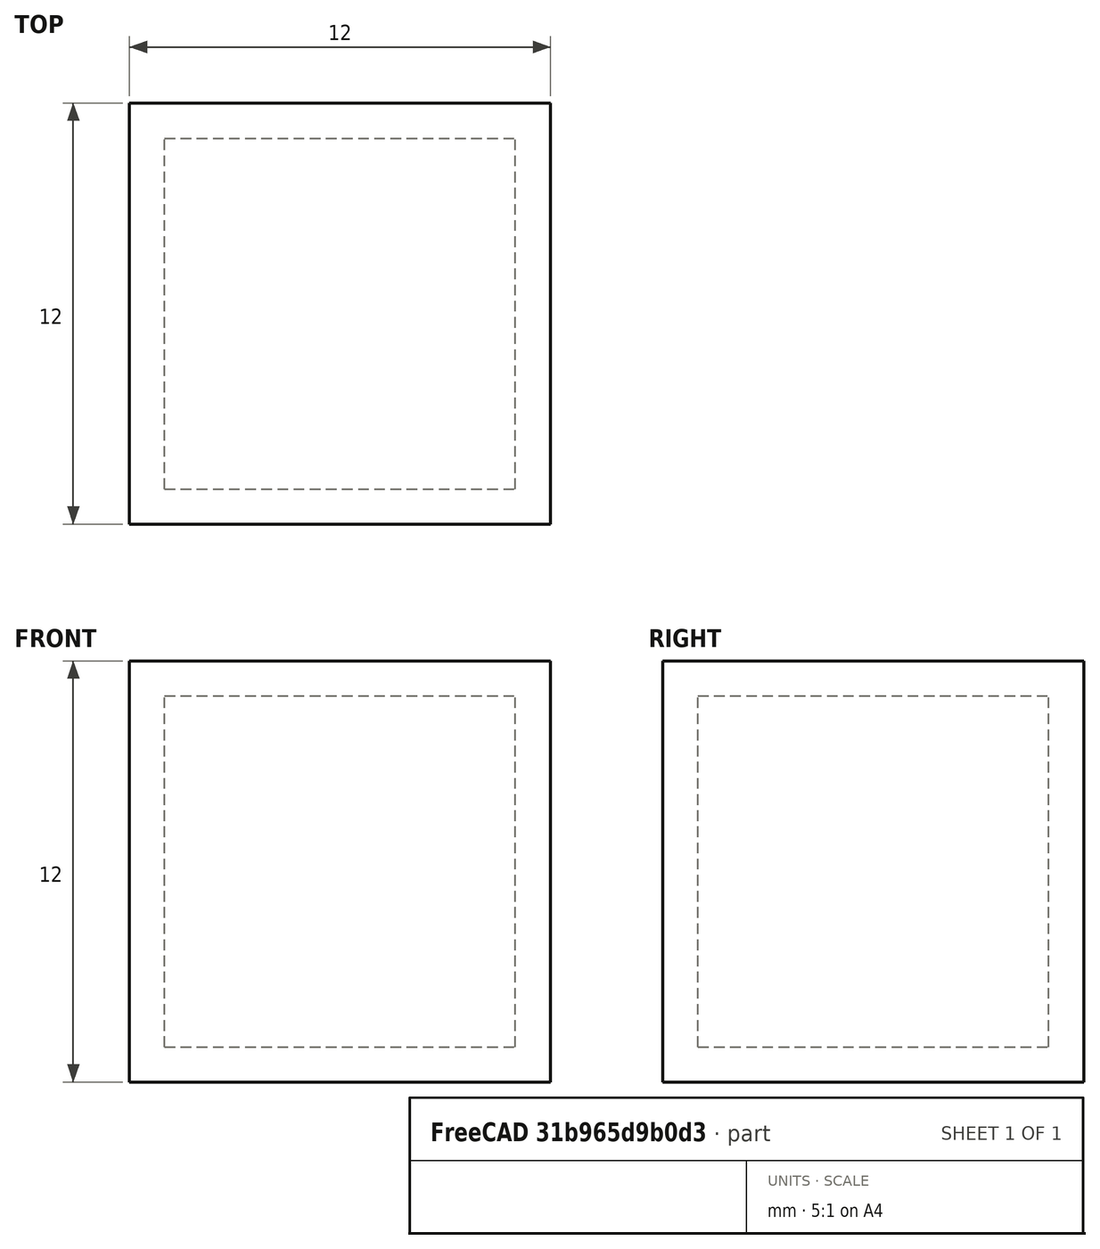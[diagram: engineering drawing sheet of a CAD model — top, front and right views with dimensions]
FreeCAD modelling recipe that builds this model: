
FCSTD DOCUMENT  (FreeCAD 0.17R12135 +10 (Git))
Label: boxtest
License: All rights reserved
LicenseURL: http://en.wikipedia.org/wiki/All_rights_reserved
objects: Path::FeaturePython×3, Part::FeaturePython×2, Part::Box×1, Path::FeatureCompoundPython×1
note: 4 computed .brp shape members not serialized (recipe doc carries the construction recipe); baked Part::Feature solids carry a one-line shape summary decoded from their .brp

FEATURE [Part::Box] Box  label="Cube"
  AttacherType = Attacher::AttachEngine3D
  Height = 10
  Length = 10
  Width = 10
FEATURE [Part::FeaturePython] Clone  label="Base-Cube"  # Draft clone (typed FeaturePython)
  AttacherType = Attacher::AttachEngine3D
  Objects = -> [Box]
  PathResource = Base
  Scale = (1,1,1)
FEATURE [Path::FeaturePython] Default_Tool  label="Default Tool"  # Path/CAM operation (typed FeaturePython)
  HorizFeed = 0
  HorizRapid = 0
  SpindleDir = 0
  SpindleSpeed = 0
  ToolNumber = 1
  VertFeed = 0
  VertRapid = 0
FEATURE [Part::FeaturePython] Stock  # WARN: FeaturePython — macro-defined, semantics opaque (R4)
  Base = -> Box
  ExtXneg = 1
  ExtXpos = 1
  ExtYneg = 1
  ExtYpos = 1
  ExtZneg = 1
  ExtZpos = 1
  StockType = FromBase
FEATURE [Path::FeaturePython] Contour  # Path/CAM operation (typed FeaturePython)
  Active = true
  AreaParams:
    OpenMode = 0
    Angle = 45.0
    MinArcPoints = 4
    Coplanar = 2
    Tolerance = 1e-07
    CleanDistance = 0.0
    PocketExtraOffset = 0.0
    AngleShift = 0.0
    SubjectFill = 0
    RoundPreceision = 0.0
    Simplify = False
    SectionTolerance = 1e-06
    MaxArcPoints = 100
    SectionOffset = 0.0
    Offset = 0.0
    Accuracy = 0.01
    PocketStepover = 0.0
    ClipFill = 0
    ToolRadius = 1.0
    Outline = False
    ClipperScale = 10000000.0
    FromCenter = True
    Explode = False
    EndType = 0
    Shift = 0.0
    ExtraPass = 0
    Project = False
    JoinType = 0
    Thicken = False
    Stepdown = 1.0
    SectionMode = 2
    MiterLimit = 2.0
    Deflection = 0.01
    Reorient = True
    FitArcs = True
    SectionCount = -1
    PocketMode = 0
    Stepover = 0.0
    Unit = 1.0
    Fill = 0
  ClearanceHeight = 15
  Direction = 0
  FinalDepth = 0
  JoinType = 0
  MiterLimit = 0.1
  OffsetExtra = 0
  PathParams = {'resume_height': 1.0, 'feedrate': 0.0, 'verbose': True, 'orientation': 1, 'return_end': True, 'preamble': False, 'retraction': 15.0, 'feedrate_v': 0.0}
  SafeHeight = 13
  Side = 0
  StartDepth = 10
  StartPoint = (0,0,0)
  StepDown = 1
  ToolController = -> Default_Tool
  UseComp = false
  UseStartPoint = false
FEATURE [Path::FeatureCompoundPython] Operations  # Path/CAM operation (typed FeaturePython)
  Group = -> [Contour]
  UsePlacements = false
FEATURE [Path::FeaturePython] Job  # Path/CAM operation (typed FeaturePython)
  Base = -> Clone
  GeometryTolerance = 0.01
  Operations = -> Operations
  PostProcessor = 2
  PostProcessorArgs = --no-header --no-line-numbers --no-comments --no-show-editor --precision=2 --inches
  Stock = -> Stock
  ToolController = -> [Default_Tool]
